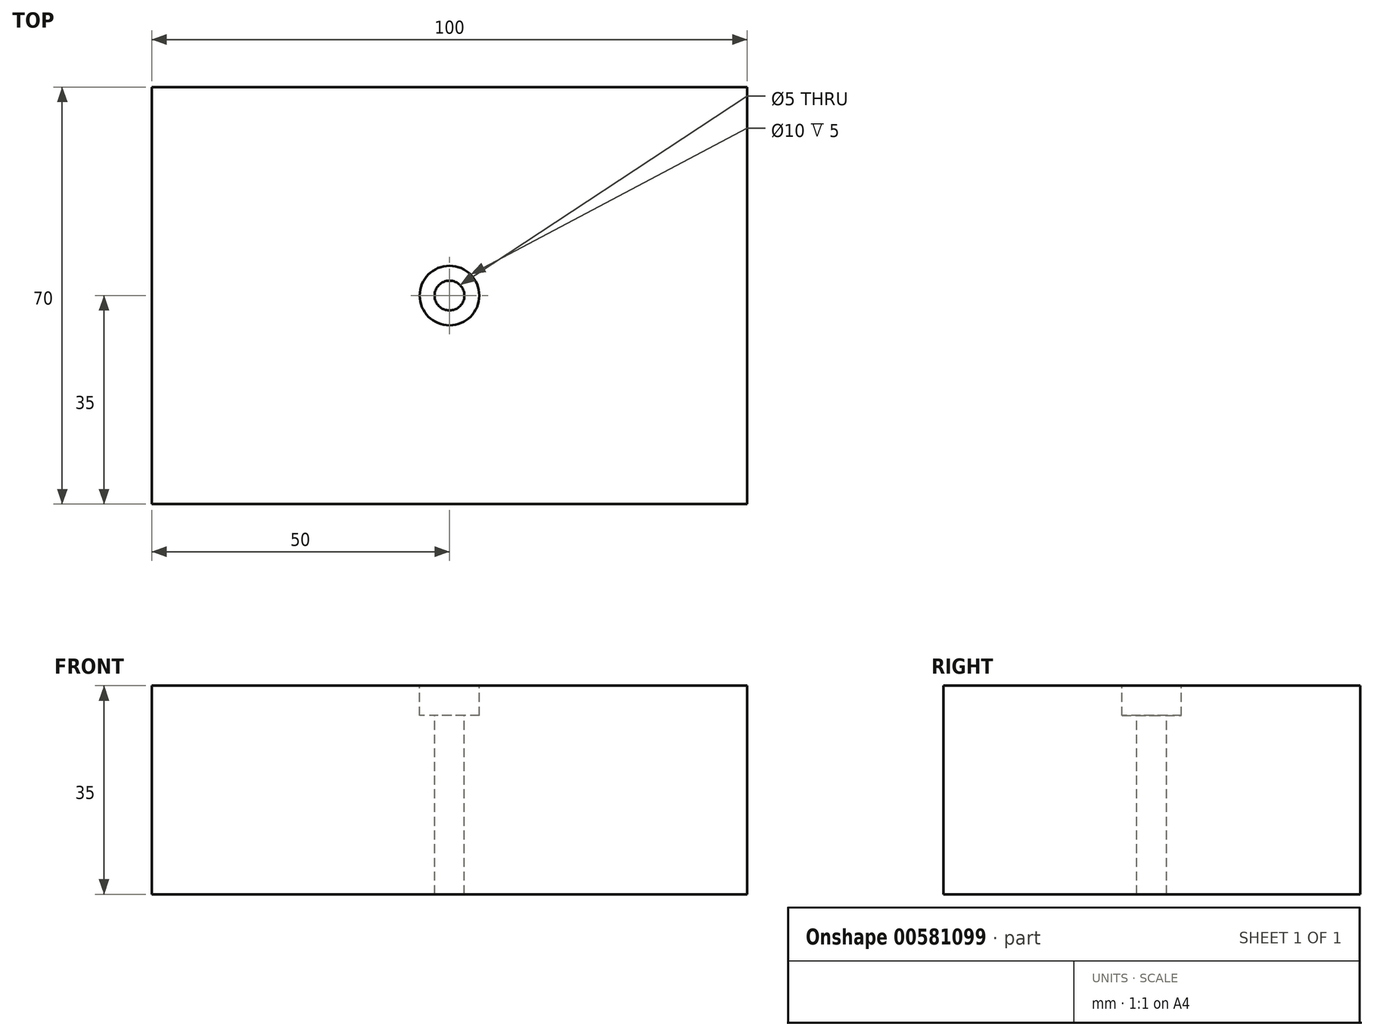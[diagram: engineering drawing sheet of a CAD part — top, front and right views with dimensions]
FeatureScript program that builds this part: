
annotation { "Feature Type Name" : "Feature", "Feature Type Description" : "" }
export const myFeature = defineFeature(function(context is Context, id is Id, definition is map)
    precondition{}
    {
        {
            var Q0;
            Q0=qCreatedBy(makeId("Top.planeOp"),FACE);
            var sketch = newSketch(context, id + "F0", { "sketchPlane" : qUnion([Q0])});
            skLineSegment(sketch, "E0.bottom", {"start": v(50, -35) * mm, "end": v(-50, -35) * mm});
            skLineSegment(sketch, "E0.top", {"start": v(50, 35) * mm, "end": v(-50, 35) * mm});
            skLineSegment(sketch, "E0.left", {"start": v(50, -35) * mm, "end": v(50, 35) * mm});
            skLineSegment(sketch, "E0.right", {"start": v(-50, -35) * mm, "end": v(-50, 35) * mm});
            skPoint(sketch, "E0.middle", {"position": v(0, 0) * mm});
            skSolve(sketch);
        }
        {
            var Q0;
            Q0 = qSketchRegion(id + "F0", true);
            extrude(context, id + "F1", {"entities" : qUnion([Q0]), "endBound" : BoundingType.SYMMETRIC, "depth" : 35 * mm, "offsetDistance" : 25 * mm});
        }
        {
            var Q0;
            Q0=makeQuery(id+"F1.opExtrude","CAP_FACE",FACE,{"disambiguationData":[OSD([sQuery(id+"F0.wireOp",EDGE,"E0.bottom"),sQuery(id+"F0.wireOp",EDGE,"E0.top"),sQuery(id+"F0.wireOp",EDGE,"E0.left"),sQuery(id+"F0.wireOp",EDGE,"E0.right")])],"isStart":false});
            var sketch = newSketch(context, id + "F2", { "sketchPlane" : qUnion([Q0])});
            skSolve(sketch);
        }
        {
            var Q0;
            Q0=makeQuery(id+"F2.imprint","IMPRINT",FACE,{"disambiguationData":[TD([[makeQuery(id+"F2.imprint","IMPRINT",EDGE,{"derivedFrom":makeQuery(id+"F1.opExtrude","CAP_EDGE",EDGE,{"disambiguationData":[OSD([sQuery(id+"F0.wireOp",EDGE,"E0.bottom")])],"isStart":false})}),-1.0]])]});
            var sketch = newSketch(context, id + "F3", { "sketchPlane" : qUnion([Q0])});
            skPoint(sketch, "E1", {"position": v(0, 0) * mm});
            skSolve(sketch);
        }
        {
            var Q0;
            Q0=sQuery(id+"F3.wireOp",VERTEX,"E1");
            var Q1;
            Q1=makeQuery(id+"F1.opExtrude","SWEPT_BODY",BODY,{"disambiguationData":[OSD([sQuery(id+"F0.wireOp",EDGE,"E0.bottom"),sQuery(id+"F0.wireOp",EDGE,"E0.top"),sQuery(id+"F0.wireOp",EDGE,"E0.left"),sQuery(id+"F0.wireOp",EDGE,"E0.right")])]});
            hole(context, id + "F4", {"style" : HoleStyle.C_BORE, "endStyle" : HoleEndStyle.THROUGH, "holeDiameter" : 5 * mm, "cBoreDiameter" : 10 * mm, "cBoreDepth" : 5 * mm, "majorDiameter" : 5 * mm, "isTappedThrough" : true, "tappedDepth" : 12 * mm, "tapClearance" : 3, "locations" : qUnion([Q0]), "scope" : qUnion([Q1])});
        }
    });
